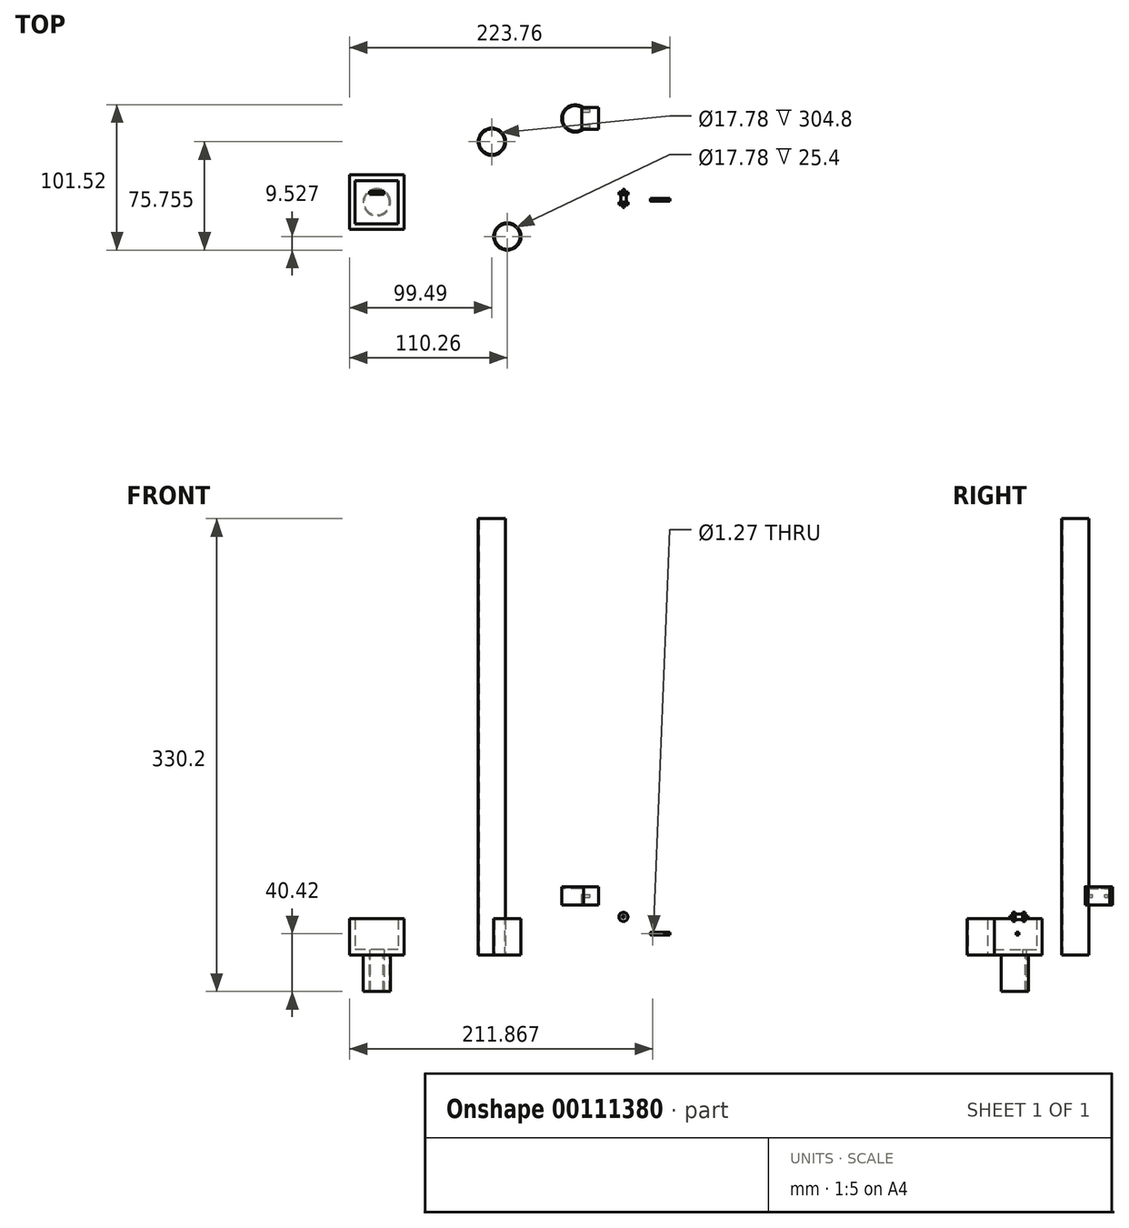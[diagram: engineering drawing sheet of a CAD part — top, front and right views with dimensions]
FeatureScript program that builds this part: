
annotation { "Feature Type Name" : "Feature", "Feature Type Description" : "" }
export const myFeature = defineFeature(function(context is Context, id is Id, definition is map)
    precondition{}
    {
        {
            var Q0;
            Q0=qCreatedBy(makeId("Top.planeOp"),FACE);
            var sketch = newSketch(context, id + "F0", { "sketchPlane" : qUnion([Q0])});
            skCircle(sketch, "E0", {"center": v(-57.88, -26.77) * mm, "radius": 9.53 * mm});
            skCircle(sketch, "E1", {"center": v(-57.88, -26.77) * mm, "radius": 8.9 * mm});
            skSolve(sketch);
        }
        {
            var Q0;
            Q0 = qSketchRegion(id + "F0", true);
            extrude(context, id + "F1", {"entities" : qUnion([Q0]), "depth" : 25.4 * mm});
        }
        {
            var Q0;
            Q0=qCreatedBy(makeId("Front.planeOp"),FACE);
            var sketch = newSketch(context, id + "F2", { "sketchPlane" : qUnion([Q0])});
            skCircle(sketch, "E2", {"center": v(23.21, 26.77) * mm, "radius": 3.18 * mm});
            skCircle(sketch, "E3", {"center": v(23.21, 26.77) * mm, "radius": 1.9 * mm});
            skCircle(sketch, "E4", {"center": v(23.21, 26.77) * mm, "radius": 0.64 * mm});
            skSolve(sketch);
        }
        {
            var Q0;
            Q0=makeQuery(id+"F2.imprint","IMPRINT",FACE,{"disambiguationData":[TD([[makeQuery(id+"F2.imprint","IMPRINT",EDGE,{"derivedFrom":sQuery(id+"F2.wireOp",EDGE,"E4")}),1.0]])]});
            extrude(context, id + "F3", {"entities" : qUnion([Q0]), "endBound" : BoundingType.SYMMETRIC, "depth" : 12.7 * mm});
        }
        {
            var Q0;
            Q0=makeQuery(id+"F2.imprint","IMPRINT",FACE,{"disambiguationData":[TD([[makeQuery(id+"F2.imprint","IMPRINT",EDGE,{"derivedFrom":sQuery(id+"F2.wireOp",EDGE,"E2")}),1.0]])]});
            var Q1;
            Q1=makeQuery(id+"F2.imprint","IMPRINT",FACE,{"disambiguationData":[TD([[makeQuery(id+"F2.imprint","IMPRINT",EDGE,{"derivedFrom":sQuery(id+"F2.wireOp",EDGE,"E3")}),1.0]])]});
            extrude(context, id + "F4", {"entities" : qUnion([Q0, Q1]), "operationType" : NewBodyOperationType.ADD, "endBound" : BoundingType.SYMMETRIC, "depth" : 8.9 * mm});
        }
        {
            var Q0;
            Q0 = qSketchRegion(id + "F2", true);
            extrude(context, id + "F5", {"entities" : qUnion([Q0]), "operationType" : NewBodyOperationType.REMOVE, "endBound" : BoundingType.SYMMETRIC, "oppositeDirection" : true, "depth" : 5.08 * mm});
        }
        {
            var Q0;
            Q0=qCreatedBy(makeId("Front.planeOp"),FACE);
            var sketch = newSketch(context, id + "F6", { "sketchPlane" : qUnion([Q0])});
            skLineSegment(sketch, "E5.bottom", {"start": v(42.5, 14.07) * mm, "end": v(55.62, 14.07) * mm});
            skLineSegment(sketch, "E5.top", {"start": v(42.5, 15.97) * mm, "end": v(55.62, 15.97) * mm});
            skLineSegment(sketch, "E5.left", {"start": v(42, 14.58) * mm, "end": v(42, 15.46) * mm});
            skLineSegment(sketch, "E5.right", {"start": v(55.62, 14.07) * mm, "end": v(55.62, 15.97) * mm});
            skPoint(sketch, "E5.middle", {"position": v(48.8, 15.02) * mm});
            skCircle(sketch, "E6", {"center": v(43.73, 15.02) * mm, "radius": 0.64 * mm});
            skPoint(sketch, "E7.visualSharp", {"position": v(42, 15.97) * mm});
            skArc(sketch, "E7.filletArc", {"start": v(42.5, 15.97) * mm, "mid": v(42.15, 15.82) * mm, "end": v(42, 15.46) * mm});
            skPoint(sketch, "E8.visualSharp", {"position": v(42, 14.07) * mm});
            skArc(sketch, "E8.filletArc", {"start": v(42, 14.58) * mm, "mid": v(42.15, 14.22) * mm, "end": v(42.5, 14.07) * mm});
            skSolve(sketch);
        }
        {
            var Q0;
            Q0 = qSketchRegion(id + "F6", true);
            extrude(context, id + "F7", {"entities" : qUnion([Q0]), "depth" : 1.93 * mm});
        }
        {
            var Q0;
            Q0=qCreatedBy(makeId("Right.planeOp"),FACE);
            var sketch = newSketch(context, id + "F8", { "sketchPlane" : qUnion([Q0])});
            skLineSegment(sketch, "E9.bottom", {"start": v(48.08, 35.1) * mm, "end": v(63.32, 35.1) * mm});
            skLineSegment(sketch, "E9.top", {"start": v(48.08, 47.8) * mm, "end": v(63.32, 47.8) * mm});
            skLineSegment(sketch, "E9.left", {"start": v(48.08, 35.1) * mm, "end": v(48.08, 47.8) * mm});
            skLineSegment(sketch, "E9.right", {"start": v(63.32, 35.1) * mm, "end": v(63.32, 47.8) * mm});
            skPoint(sketch, "E9.middle", {"position": v(55.7, 41.44) * mm});
            skLineSegment(sketch, "E10.bottom", {"start": v(49.35, 40.49) * mm, "end": v(51.28, 40.49) * mm});
            skLineSegment(sketch, "E10.top", {"start": v(49.35, 42.4) * mm, "end": v(51.28, 42.4) * mm});
            skLineSegment(sketch, "E10.left", {"start": v(49.35, 40.49) * mm, "end": v(49.35, 42.4) * mm});
            skLineSegment(sketch, "E10.right", {"start": v(51.28, 40.49) * mm, "end": v(51.28, 42.4) * mm});
            skPoint(sketch, "E10.middle", {"position": v(50.31, 41.44) * mm});
            skLineSegment(sketch, "E11.bottom", {"start": v(60.12, 40.49) * mm, "end": v(62.05, 40.49) * mm});
            skLineSegment(sketch, "E11.top", {"start": v(60.12, 42.4) * mm, "end": v(62.05, 42.4) * mm});
            skLineSegment(sketch, "E11.left", {"start": v(60.12, 40.49) * mm, "end": v(60.12, 42.4) * mm});
            skLineSegment(sketch, "E11.right", {"start": v(62.05, 40.49) * mm, "end": v(62.05, 42.4) * mm});
            skPoint(sketch, "E11.middle", {"position": v(61.08, 41.44) * mm});
            skSolve(sketch);
        }
        {
            var Q0;
            Q0 = qSketchRegion(id + "F8", true);
            extrude(context, id + "F9", {"entities" : qUnion([Q0]), "oppositeDirection" : true, "depth" : 6 * mm});
        }
        {
            var Q0;
            Q0=makeQuery(id+"F8.imprint","IMPRINT",FACE,{"disambiguationData":[TD([[makeQuery(id+"F8.imprint","IMPRINT",EDGE,{"derivedFrom":sQuery(id+"F8.wireOp",EDGE,"E10.bottom")}),1.0]])]});
            var Q1;
            Q1=makeQuery(id+"F8.imprint","IMPRINT",FACE,{"disambiguationData":[TD([[makeQuery(id+"F8.imprint","IMPRINT",EDGE,{"derivedFrom":sQuery(id+"F8.wireOp",EDGE,"E11.bottom")}),1.0]])]});
            var Q2;
            Q2=makeQuery(id+"F8.imprint","IMPRINT",FACE,{"disambiguationData":[TD([[makeQuery(id+"F8.imprint","IMPRINT",EDGE,{"derivedFrom":sQuery(id+"F8.wireOp",EDGE,"E9.bottom")}),1.0]])]});
            extrude(context, id + "F10", {"entities" : qUnion([Q0, Q1, Q2]), "operationType" : NewBodyOperationType.ADD, "depth" : 6 * mm});
        }
        {
            var Q0;
            {var subQ0=sQuery(id+"F8.wireOp",EDGE,"E9.top");Q0=makeQuery(id+"F10.boolean.opBoolean","MERGE",FACE,{"derivedFrom":[makeQuery(id+"F9.opExtrude","SWEPT_FACE",FACE,{"disambiguationData":[OSD([subQ0])]}),makeQuery(id+"F10.opExtrude","SWEPT_FACE",FACE,{"disambiguationData":[OSD([subQ0])]})]});}
            var sketch = newSketch(context, id + "F11", { "sketchPlane" : qUnion([Q0])});
            skCircle(sketch, "E12", {"center": v(-10.45, 55.7) * mm, "radius": 9.53 * mm});
            skPoint(sketch, "E12.centerSnap0", {"position": v(-6, 55.7) * mm});
            skCircle(sketch, "E13", {"center": v(-10.45, 55.7) * mm, "radius": 8.9 * mm});
            skPoint(sketch, "E14", {"position": v(-5.87, 63.32) * mm});
            skPoint(sketch, "E15", {"position": v(-4.73, 63.32) * mm});
            skPoint(sketch, "E16", {"position": v(-5.87, 48.08) * mm});
            skPoint(sketch, "E17", {"position": v(-4.73, 48.08) * mm});
            skLineSegment(sketch, "E18", {"start": v(-5.87, 48.08) * mm, "end": v(-4.73, 48.08) * mm});
            skLineSegment(sketch, "E19", {"start": v(-5.87, 63.32) * mm, "end": v(-4.73, 63.32) * mm});
            skSolve(sketch);
        }
        {
            var Q0;
            {var subQ0=sQuery(id+"F11.wireOp",EDGE,"E18");Q0=makeQuery(id+"F11.imprint","IMPRINT",FACE,{"disambiguationData":[TD([[makeQuery(id+"F11.imprint","IMPRINT",EDGE,{"derivedFrom":subQ0}),-1.0]])]});}
            extrude(context, id + "F12", {"entities" : qUnion([Q0]), "oppositeDirection" : true, "depth" : 12.7 * mm});
        }
        {
            var Q0;
            {var subQ2=sQuery(id+"F8.wireOp",EDGE,"E9.top");var subQ8=makeQuery(id+"F9.opExtrude","CAP_EDGE",EDGE,{"disambiguationData":[OSD([subQ2])],"isStart":false});Q0=makeQuery(id+"F11.imprint","IMPRINT",FACE,{"disambiguationData":[TD([[makeQuery(id+"F11.imprint","IMPRINT",EDGE,{"derivedFrom":subQ8}),1.0]])]});}
            extrude(context, id + "F13", {"entities" : qUnion([Q0]), "oppositeDirection" : true, "depth" : 19.05 * mm - 17.78 * mm});
        }
        {
            var Q0;
            Q0=qCreatedBy(makeId("Top.planeOp"),FACE);
            var sketch = newSketch(context, id + "F14", { "sketchPlane" : qUnion([Q0])});
            skLineSegment(sketch, "E20.bottom", {"start": v(-130.04, -21.88) * mm, "end": v(-168.14, -21.88) * mm});
            skLineSegment(sketch, "E20.top", {"start": v(-130.04, 16.22) * mm, "end": v(-168.14, 16.22) * mm});
            skLineSegment(sketch, "E20.left", {"start": v(-130.04, -21.88) * mm, "end": v(-130.04, 16.22) * mm});
            skLineSegment(sketch, "E20.right", {"start": v(-168.14, -21.88) * mm, "end": v(-168.14, 16.22) * mm});
            skPoint(sketch, "E20.middle", {"position": v(-149.09, -2.83) * mm});
            skCircle(sketch, "E21", {"center": v(-149.09, -2.83) * mm, "radius": 9.53 * mm});
            skCircle(sketch, "E22", {"center": v(-149.09, -2.83) * mm, "radius": 8.9 * mm});
            skLineSegment(sketch, "E23.bottom", {"start": v(-134.04, -17.88) * mm, "end": v(-164.14, -17.88) * mm});
            skLineSegment(sketch, "E23.top", {"start": v(-134.04, 12.22) * mm, "end": v(-164.14, 12.22) * mm});
            skLineSegment(sketch, "E23.left", {"start": v(-164.14, -17.88) * mm, "end": v(-164.14, 12.22) * mm});
            skLineSegment(sketch, "E23.right", {"start": v(-134.04, -17.88) * mm, "end": v(-134.04, 12.22) * mm});
            skLineSegment(sketch, "E24.bottom", {"start": v(-144.09, 2.6) * mm, "end": v(-154.09, 2.6) * mm});
            skLineSegment(sketch, "E24.top", {"start": v(-144.09, 4.94) * mm, "end": v(-154.09, 4.94) * mm});
            skLineSegment(sketch, "E24.left", {"start": v(-144.09, 2.6) * mm, "end": v(-144.09, 4.94) * mm});
            skLineSegment(sketch, "E24.right", {"start": v(-154.09, 2.6) * mm, "end": v(-154.09, 4.94) * mm});
            skPoint(sketch, "E24.middle", {"position": v(-149.09, 3.78) * mm});
            skSolve(sketch);
        }
        {
            var Q0;
            Q0 = qSketchRegion(id + "F14", true);
            extrude(context, id + "F15", {"entities" : qUnion([Q0]), "depth" : 25.4 * mm});
        }
        {
            var Q0;
            Q0=makeQuery(id+"F14.imprint","IMPRINT",FACE,{"disambiguationData":[TD([[makeQuery(id+"F14.imprint","IMPRINT",EDGE,{"derivedFrom":sQuery(id+"F14.wireOp",EDGE,"E21")}),-1.0]])]});
            var Q1;
            Q1=makeQuery(id+"F14.imprint","IMPRINT",FACE,{"disambiguationData":[TD([[makeQuery(id+"F14.imprint","IMPRINT",EDGE,{"derivedFrom":sQuery(id+"F14.wireOp",EDGE,"E21")}),1.0]])]});
            var Q2;
            {var subQ5=sQuery(id+"F14.wireOp",EDGE,"E24.bottom");Q2=makeQuery(id+"F14.imprint","IMPRINT",FACE,{"disambiguationData":[TD([[makeQuery(id+"F14.imprint","IMPRINT",EDGE,{"derivedFrom":subQ5}),1.0]])]});}
            var Q3;
            {var subQ0=sQuery(id+"F14.wireOp",EDGE,"E24.top");var subQ1=sQuery(id+"F14.wireOp",EDGE,"E22");var subQ2=makeQuery(id+"F14.imprint","INTERSECT",VERTEX,{"disambiguationData":[OD(0.0)],"derivedFrom":[subQ1,subQ0]});Q3=makeQuery(id+"F14.imprint","IMPRINT",FACE,{"disambiguationData":[TD([[makeQuery(id+"F14.imprint","IMPRINT",EDGE,{"disambiguationData":[TD([[subQ2,-1.0]])],"derivedFrom":subQ1}),1.0]])]});}
            extrude(context, id + "F16", {"entities" : qUnion([Q0, Q1, Q2, Q3]), "operationType" : NewBodyOperationType.ADD, "depth" : 4 * mm});
        }
        {
            var Q0;
            Q0=makeQuery(id+"F14.imprint","IMPRINT",FACE,{"disambiguationData":[TD([[makeQuery(id+"F14.imprint","IMPRINT",EDGE,{"derivedFrom":sQuery(id+"F14.wireOp",EDGE,"E21")}),1.0]])]});
            extrude(context, id + "F17", {"entities" : qUnion([Q0]), "operationType" : NewBodyOperationType.ADD, "oppositeDirection" : true, "depth" : 25.4 * mm});
        }
        {
            var Q0;
            Q0=qCreatedBy(makeId("Top.planeOp"),FACE);
            var sketch = newSketch(context, id + "F18", { "sketchPlane" : qUnion([Q0])});
            skCircle(sketch, "E25", {"center": v(-68.65, 39.46) * mm, "radius": 9.53 * mm});
            skCircle(sketch, "E26", {"center": v(-68.65, 39.46) * mm, "radius": 8.9 * mm});
            skSolve(sketch);
        }
        {
            var Q0;
            Q0 = qSketchRegion(id + "F18", true);
            extrude(context, id + "F19", {"entities" : qUnion([Q0]), "depth" : 304.8 * mm});
        }
    });
